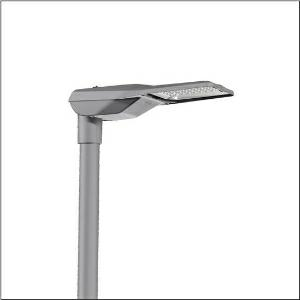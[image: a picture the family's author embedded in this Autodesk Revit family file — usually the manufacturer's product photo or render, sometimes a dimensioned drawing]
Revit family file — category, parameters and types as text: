
# Revit family: streetlight_sl_21_iq_mini___st1_0a_5xe2d31v08gb_747e
name_source: partatom
category: Lighting Fixtures
units: mm (PartAtom-declared; Revit-internal decimal feet)

## family parameters
Cut with Voids When Loaded = No
Host = Face
Light Source = No
Part Type = Normal
Room Calculation Point = No
Round Connector Dimension = Use Diameter
Shared = No

## types (1)
- --- (1 x LED, 5990 lm, 39.8 W, 3000K)
    Apparent Load = 40 VA
    CIE Flux Codes = 37 72 97 100 100
    Color Rendering = 70
    Color Temperature = 3000K
    Default Elevation = 1800 mm
    Description = Streetlight SL 21 iQ mini, mast luminaire, primary light control with lens, of PMMA, primary optical cover: cover, of toughened safety glass, transparent, light distribution: ST1.0a, light emission: direct distribution, primary light characteristic: asymmetric, installation type: post-top, side-entry, LED, High Power LED, rated luminous flux: 5.990lm, luminous efficacy: 151lm/W, light colour: 730, colour temperature: 3000K, control gear: iQ-Street Remote, D4i with power reduction, control: pre-setting: logarithmic dimming characteristic, Street-Remote, Auto-Match, Temp-Guard, Lumen-Switch, Night-Set, Smart-Wire, Light-Fading, Desk-Remote (wireless, voltage-free reading and setting of iQ features in the workshop via application-optimized NFC function/RFID function), optimised constant luminous flux control (CLO 2.0), mains connection: 220..240V, AC, 50/60Hz, start of lifetime: 40W, end of service life: 41W, reduction: 18W, luminaire housing, of diecast aluminium, powder-coated, SITECO metallic grey (DB 702S), corrosivity category C5 high according to DIN EN ISO 12944, please order mast flange separately, inclination adjustable: 0°, 5°, 10°, 15°, sealing non-destructively replaceable, multi-level sealing system, length: 628mm, width: 235mm, height: 110mm, mast flange for spigot size: 42mm (side-entry): 5XC10008XM4, 60/48mm (side-entry/post-top): 5XC10108XM2, 76/60mm (side-entry/post-top): 5XC10108XM1, mounting height: 4..8m, Smart Interface above, protection rating (complete): IP66, insulation class (complete): insulation class II (safety insulation), certification: CE, ENEC, ENEC+, VDE, impact resistance: IK10, permissible operating ambient temperature for outdoor applications: -40..+50°C, standard-compliant lighting for roads and squares, packaging unit: 1 piece

Light Distribution: ST1.0a
    Height = 110 mm
    Lamp = 1 x LED
    Lamp Light Flux = 5990 lm
    Lamp Power = 39.8 W
    Lamp count = 1
    Length = 625 mm
    Luminous efficacy = 151 lm/W
    Manufacturer = Siteco
    ModVariant = No
    Model = 5XE2D31V08GB
    Number of Poles = 1
    OnlyDefault = Yes
    Power Factor = 1
    Product Name = Streetlight SL 21 iQ mini | ST1.0a
    Product group = mast luminaire | pylon top
    ProductGroupID = 6100
    Protection Class = Protection class II
    Protection Degree = IP 66
    RLX_Detail_Level = 1
    RLX_Emergency_Light_Flux = 0 lm
    RLX_Emergency_Type = 0
    RLX_Emergency_Type_DB = No
    RlxData = <blob elided: 92713 chars, md5=293aa6f9>
    Socket = socket
    Standby Power = 0 W
    System Light Flux = 5990 lm
    System Power = 40 W
    Type Comments = factory setting: luminous flux: 100 % | dim-lin: 254 | 800 mA
    Type Image = l_1003515.jpg
    URL = http://relux.com
    VarID = @adj_115271
    Voltage = 0 V
    Weight = 0.00 kg
    Width = 234 mm

## geometry (parser evidence)
native form markers: Blend x4, Sweep x11
no freeform markers — native parametric forms only
